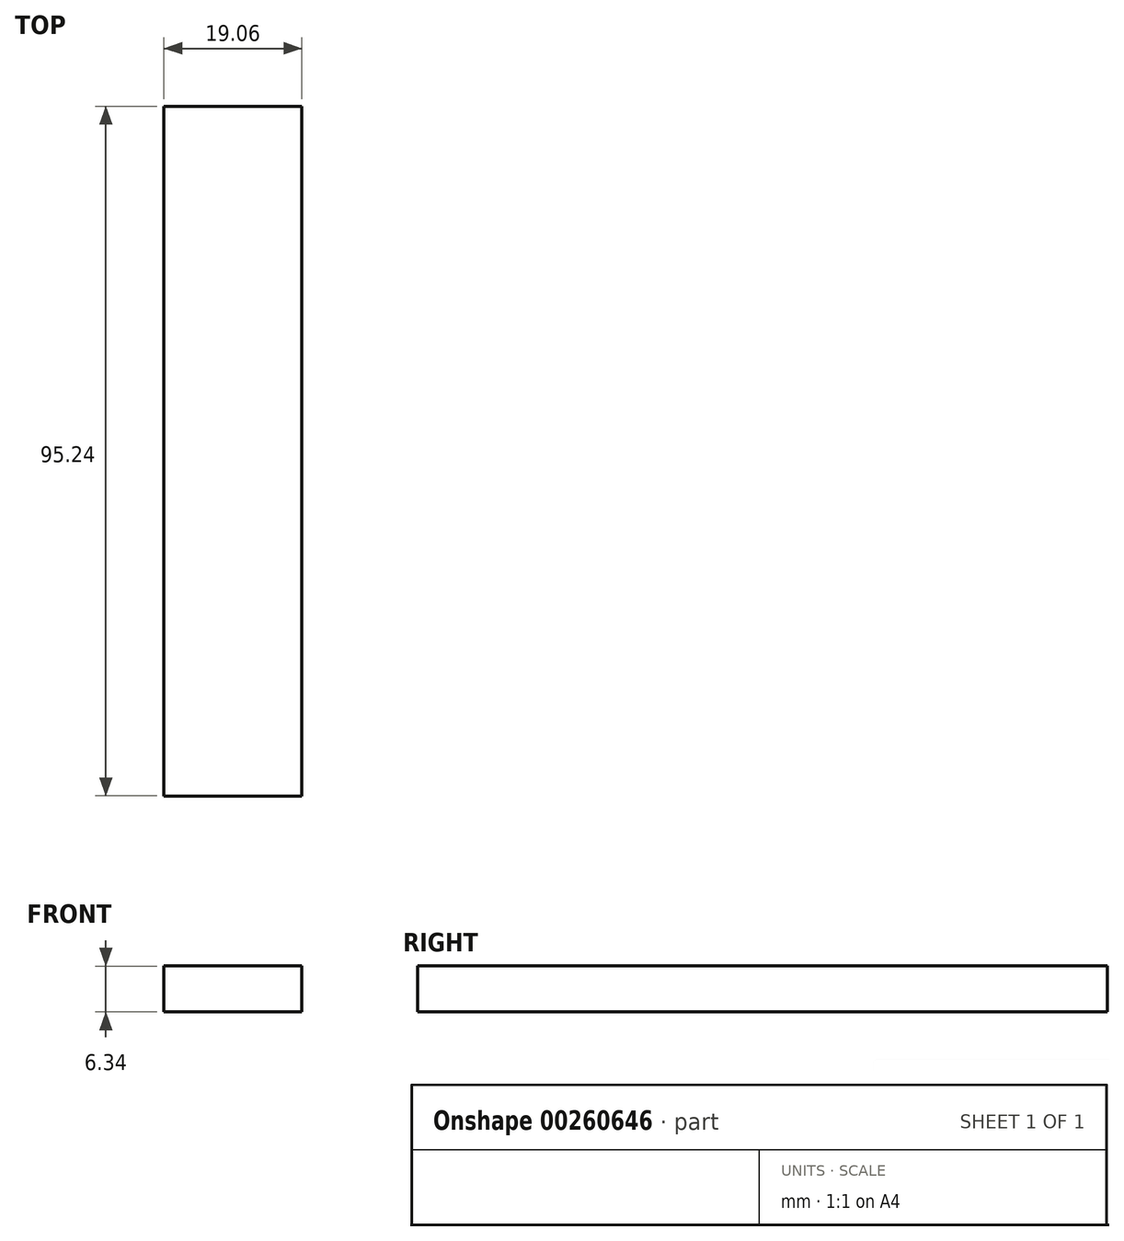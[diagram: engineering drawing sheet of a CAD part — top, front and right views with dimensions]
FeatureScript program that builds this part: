
annotation { "Feature Type Name" : "Feature", "Feature Type Description" : "" }
export const myFeature = defineFeature(function(context is Context, id is Id, definition is map)
    precondition{}
    {
        {
            var Q0;
            Q0=qCreatedBy(makeId("Front.planeOp"),FACE);
            var sketch = newSketch(context, id + "F0", { "sketchPlane" : qUnion([Q0])});
            skLineSegment(sketch, "E0.bottom", {"start": v(-9.53, 3.18) * mm, "end": v(9.53, 3.18) * mm});
            skLineSegment(sketch, "E0.top", {"start": v(-9.53, -3.18) * mm, "end": v(9.53, -3.18) * mm});
            skLineSegment(sketch, "E0.left", {"start": v(-9.53, 3.18) * mm, "end": v(-9.53, -3.17) * mm});
            skLineSegment(sketch, "E0.right", {"start": v(9.53, 3.18) * mm, "end": v(9.53, -3.17) * mm});
            skPoint(sketch, "E0.middle", {"position": v(0, 0) * mm});
            skSolve(sketch);
        }
        {
            var Q0;
            Q0 = qSketchRegion(id + "F0", true);
            extrude(context, id + "F1", {"entities" : qUnion([Q0]), "endBound" : BoundingType.SYMMETRIC, "depth" : 95.25 * mm});
        }
    });
